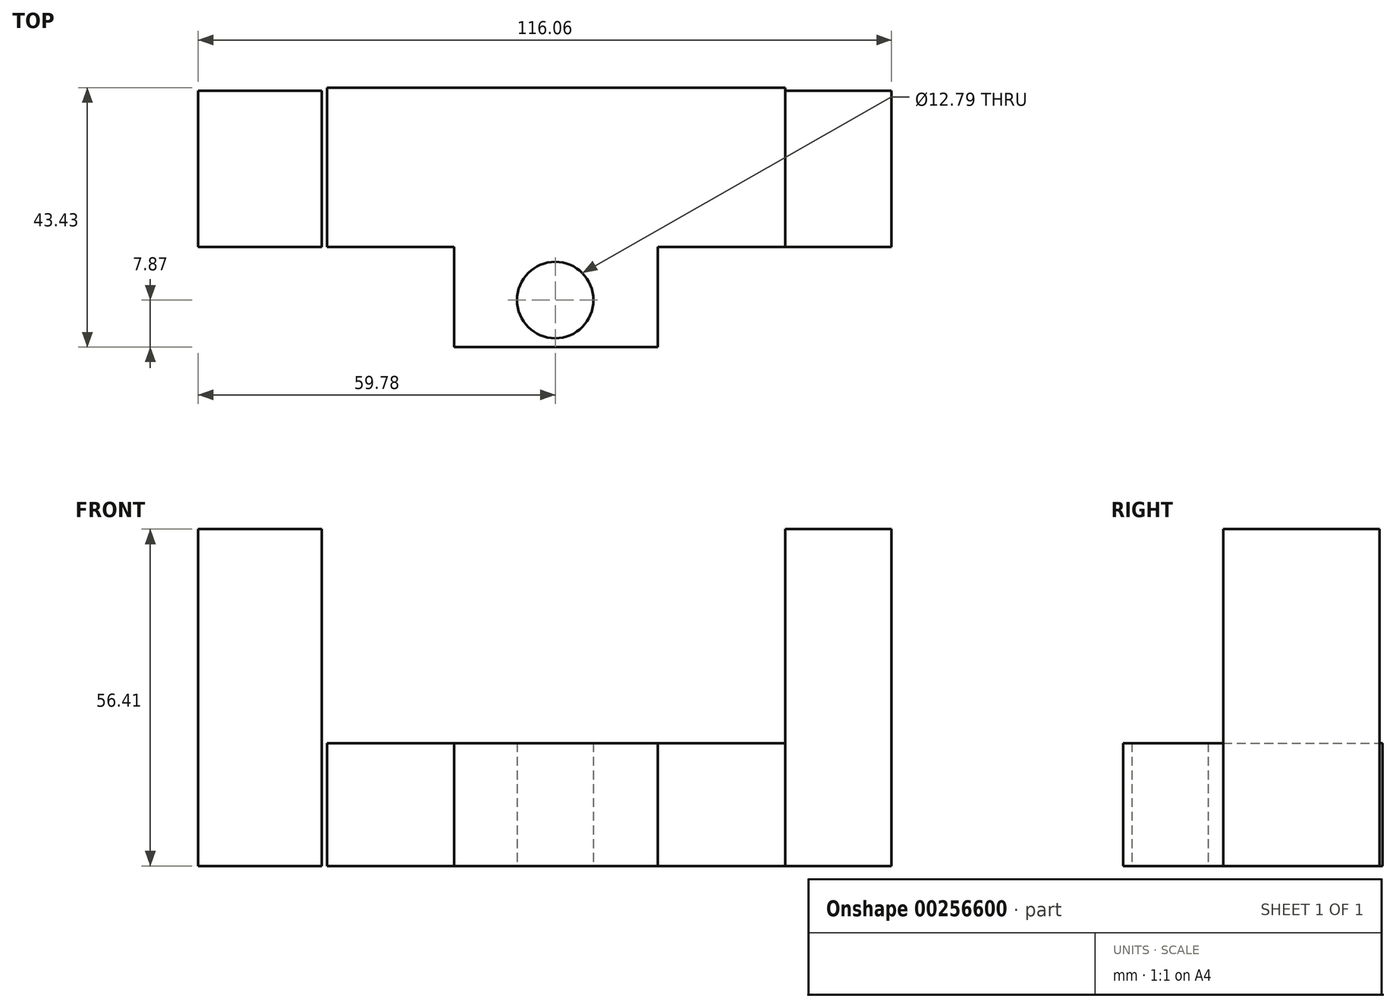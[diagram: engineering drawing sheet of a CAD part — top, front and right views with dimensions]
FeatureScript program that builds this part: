
annotation { "Feature Type Name" : "Feature", "Feature Type Description" : "" }
export const myFeature = defineFeature(function(context is Context, id is Id, definition is map)
    precondition{}
    {
        {
            var Q0;
            Q0=qCreatedBy(makeId("Top.planeOp"),FACE);
            var sketch = newSketch(context, id + "F0", { "sketchPlane" : qUnion([Q0])});
            skLineSegment(sketch, "E0.bottom", {"start": v(-16.9, 0) * mm, "end": v(17.2, 0) * mm});
            skLineSegment(sketch, "E0.top", {"start": v(-16.9, -16.76) * mm, "end": v(17.2, -16.76) * mm});
            skLineSegment(sketch, "E0.left", {"start": v(-16.9, 0) * mm, "end": v(-16.9, -16.76) * mm});
            skLineSegment(sketch, "E0.right", {"start": v(17.2, 0) * mm, "end": v(17.2, -16.76) * mm});
            skLineSegment(sketch, "E1.bottom", {"start": v(-38.18, 0) * mm, "end": v(38.47, 0) * mm});
            skLineSegment(sketch, "E1.top", {"start": v(-38.18, 26.67) * mm, "end": v(38.47, 26.67) * mm});
            skLineSegment(sketch, "E1.left", {"start": v(-38.18, 0) * mm, "end": v(-38.18, 26.67) * mm});
            skLineSegment(sketch, "E1.right", {"start": v(38.47, 0) * mm, "end": v(38.47, 26.67) * mm});
            skSolve(sketch);
        }
        {
            var Q0;
            Q0 = qSketchRegion(id + "F0", true);
            extrude(context, id + "F1", {"entities" : qUnion([Q0]), "depth" : 20.57 * mm});
        }
        {
            var Q0;
            Q0=qCreatedBy(makeId("Front.planeOp"),FACE);
            var sketch = newSketch(context, id + "F2", { "sketchPlane" : qUnion([Q0])});
            skLineSegment(sketch, "E2.bottom", {"start": v(-39.08, 0) * mm, "end": v(-59.78, 0) * mm});
            skLineSegment(sketch, "E2.top", {"start": v(-39.08, 56.41) * mm, "end": v(-59.78, 56.41) * mm});
            skLineSegment(sketch, "E2.left", {"start": v(-39.08, 0) * mm, "end": v(-39.08, 56.41) * mm});
            skLineSegment(sketch, "E2.right", {"start": v(-59.78, 0) * mm, "end": v(-59.78, 56.41) * mm});
            skLineSegment(sketch, "E3.bottom", {"start": v(38.5, 0) * mm, "end": v(56.28, 0) * mm});
            skLineSegment(sketch, "E3.top", {"start": v(38.5, 56.41) * mm, "end": v(56.28, 56.41) * mm});
            skLineSegment(sketch, "E3.left", {"start": v(38.5, 0) * mm, "end": v(38.5, 56.41) * mm});
            skLineSegment(sketch, "E3.right", {"start": v(56.28, 0) * mm, "end": v(56.28, 56.41) * mm});
            skSolve(sketch);
        }
        {
            var Q0;
            Q0 = qSketchRegion(id + "F2", true);
            extrude(context, id + "F3", {"entities" : qUnion([Q0]), "oppositeDirection" : true, "depth" : 26.16 * mm});
        }
        {
            var Q0;
            Q0=qCreatedBy(makeId("Top.planeOp"),FACE);
            var sketch = newSketch(context, id + "F4", { "sketchPlane" : qUnion([Q0])});
            skCircle(sketch, "E4", {"center": v(0, -8.9) * mm, "radius": 6.4 * mm});
            skSolve(sketch);
        }
        {
            var Q0;
            Q0 = qSketchRegion(id + "F4", true);
            extrude(context, id + "F5", {"entities" : qUnion([Q0]), "operationType" : NewBodyOperationType.REMOVE, "depth" : 70.36 * mm});
        }
    });
